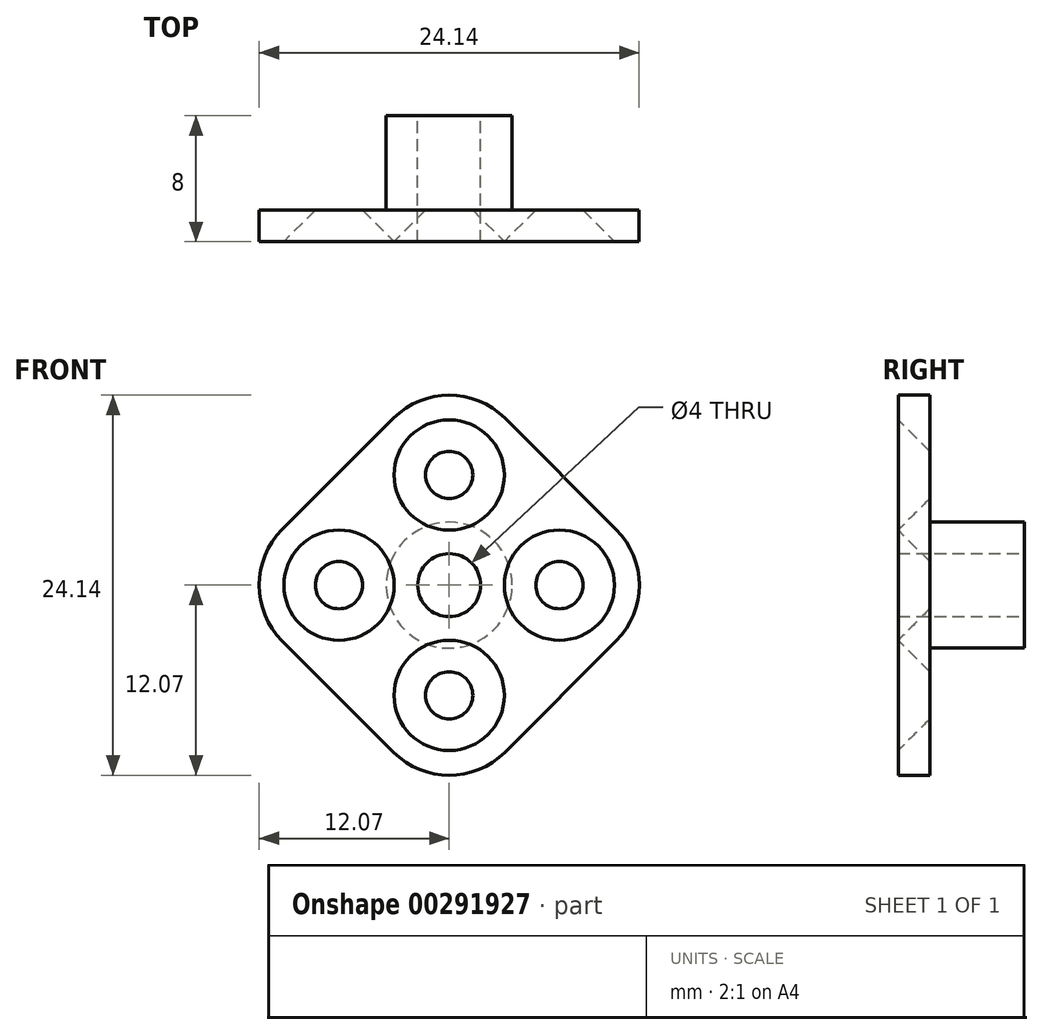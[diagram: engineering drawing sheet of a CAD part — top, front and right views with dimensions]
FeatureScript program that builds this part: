
annotation { "Feature Type Name" : "Feature", "Feature Type Description" : "" }
export const myFeature = defineFeature(function(context is Context, id is Id, definition is map)
    precondition{}
    {
        {
            var Q0;
            Q0=qCreatedBy(makeId("Front.planeOp"),FACE);
            var sketch = newSketch(context, id + "F0", { "sketchPlane" : qUnion([Q0])});
            skPoint(sketch, "E0.middle", {"position": v(0, 0) * mm});
            skCircle(sketch, "E1", {"center": v(0, 0) * mm, "radius": 2 * mm});
            skCircle(sketch, "E2", {"center": v(7, 0) * mm, "radius": 1.5 * mm});
            skCircle(sketch, "E3.1.0", {"center": v(0, 7) * mm, "radius": 1.5 * mm});
            skCircle(sketch, "E3.2.0", {"center": v(-7, 0) * mm, "radius": 1.5 * mm});
            skCircle(sketch, "E3.3.0", {"center": v(0, -7) * mm, "radius": 1.5 * mm});
            skPoint(sketch, "E4.endSnap0", {"position": v(0, -11.8) * mm});
            skLineSegment(sketch, "E5.bottom", {"start": v(-3.54, -10.6) * mm, "end": v(-10.6, -3.54) * mm});
            skLineSegment(sketch, "E5.top", {"start": v(10.6, 3.54) * mm, "end": v(3.54, 10.6) * mm});
            skLineSegment(sketch, "E5.left", {"start": v(3.54, -10.6) * mm, "end": v(10.6, -3.54) * mm});
            skLineSegment(sketch, "E5.right", {"start": v(-10.6, 3.54) * mm, "end": v(-3.54, 10.6) * mm});
            skPoint(sketch, "E6.visualSharp", {"position": v(0, -14.14) * mm});
            skArc(sketch, "E6.filletArc", {"start": v(-3.54, -10.6) * mm, "mid": v(0, -12.07) * mm, "end": v(3.54, -10.6) * mm});
            skPoint(sketch, "E7.visualSharp", {"position": v(-14.14, 0) * mm});
            skArc(sketch, "E7.filletArc", {"start": v(-10.6, 3.54) * mm, "mid": v(-12.07, 0) * mm, "end": v(-10.6, -3.54) * mm});
            skPoint(sketch, "E8.visualSharp", {"position": v(0, 14.14) * mm});
            skArc(sketch, "E8.filletArc", {"start": v(3.54, 10.6) * mm, "mid": v(0, 12.07) * mm, "end": v(-3.54, 10.6) * mm});
            skPoint(sketch, "E9.visualSharp", {"position": v(14.14, 0) * mm});
            skArc(sketch, "E9.filletArc", {"start": v(10.6, -3.54) * mm, "mid": v(12.07, 0) * mm, "end": v(10.6, 3.54) * mm});
            skSolve(sketch);
        }
        {
            var Q0;
            Q0 = qSketchRegion(id + "F0", true);
            extrude(context, id + "F1", {"entities" : qUnion([Q0]), "depth" : 2 * mm});
        }
        {
            var Q0;
            Q0=makeQuery(id+"F1.opExtrude","CAP_EDGE",EDGE,{"disambiguationData":[OSD([sQuery(id+"F0.wireOp",EDGE,"E2")])],"isStart":false});
            var Q1;
            Q1=makeQuery(id+"F1.opExtrude","CAP_EDGE",EDGE,{"disambiguationData":[OSD([sQuery(id+"F0.wireOp",EDGE,"E3.3.0")])],"isStart":false});
            var Q2;
            Q2=makeQuery(id+"F1.opExtrude","CAP_EDGE",EDGE,{"disambiguationData":[OSD([sQuery(id+"F0.wireOp",EDGE,"E3.2.0")])],"isStart":false});
            var Q3;
            Q3=makeQuery(id+"F1.opExtrude","CAP_EDGE",EDGE,{"disambiguationData":[OSD([sQuery(id+"F0.wireOp",EDGE,"E3.1.0")])],"isStart":false});
            chamfer(context, id + "F2", {"entities" : qUnion([Q0, Q1, Q2, Q3]), "width" : 2 * mm, "tangentPropagation" : true});
        }
        {
            var Q0;
            Q0=makeQuery(id+"F1.opExtrude","CAP_FACE",FACE,{"disambiguationData":[OSD([sQuery(id+"F0.wireOp",EDGE,"E1"),sQuery(id+"F0.wireOp",EDGE,"E2"),sQuery(id+"F0.wireOp",EDGE,"E3.1.0"),sQuery(id+"F0.wireOp",EDGE,"E3.2.0"),sQuery(id+"F0.wireOp",EDGE,"E3.3.0"),sQuery(id+"F0.wireOp",EDGE,"E5.bottom"),sQuery(id+"F0.wireOp",EDGE,"E5.top"),sQuery(id+"F0.wireOp",EDGE,"E5.left"),sQuery(id+"F0.wireOp",EDGE,"E5.right"),sQuery(id+"F0.wireOp",EDGE,"E6.filletArc"),sQuery(id+"F0.wireOp",EDGE,"E7.filletArc"),sQuery(id+"F0.wireOp",EDGE,"E8.filletArc"),sQuery(id+"F0.wireOp",EDGE,"E9.filletArc")])],"isStart":true});
            var sketch = newSketch(context, id + "F3", { "sketchPlane" : qUnion([Q0])});
            skCircle(sketch, "E10", {"center": v(0, 0) * mm, "radius": 4 * mm});
            skSolve(sketch);
        }
        {
            var Q0;
            Q0=makeQuery(id+"F3.imprint","IMPRINT",FACE,{"disambiguationData":[TD([[makeQuery(id+"F3.imprint","IMPRINT",EDGE,{"derivedFrom":sQuery(id+"F3.wireOp",EDGE,"E10")}),1.0]])]});
            extrude(context, id + "F4", {"entities" : qUnion([Q0]), "operationType" : NewBodyOperationType.ADD, "depth" : 6 * mm, "offsetDistance" : 25 * mm});
        }
    });
